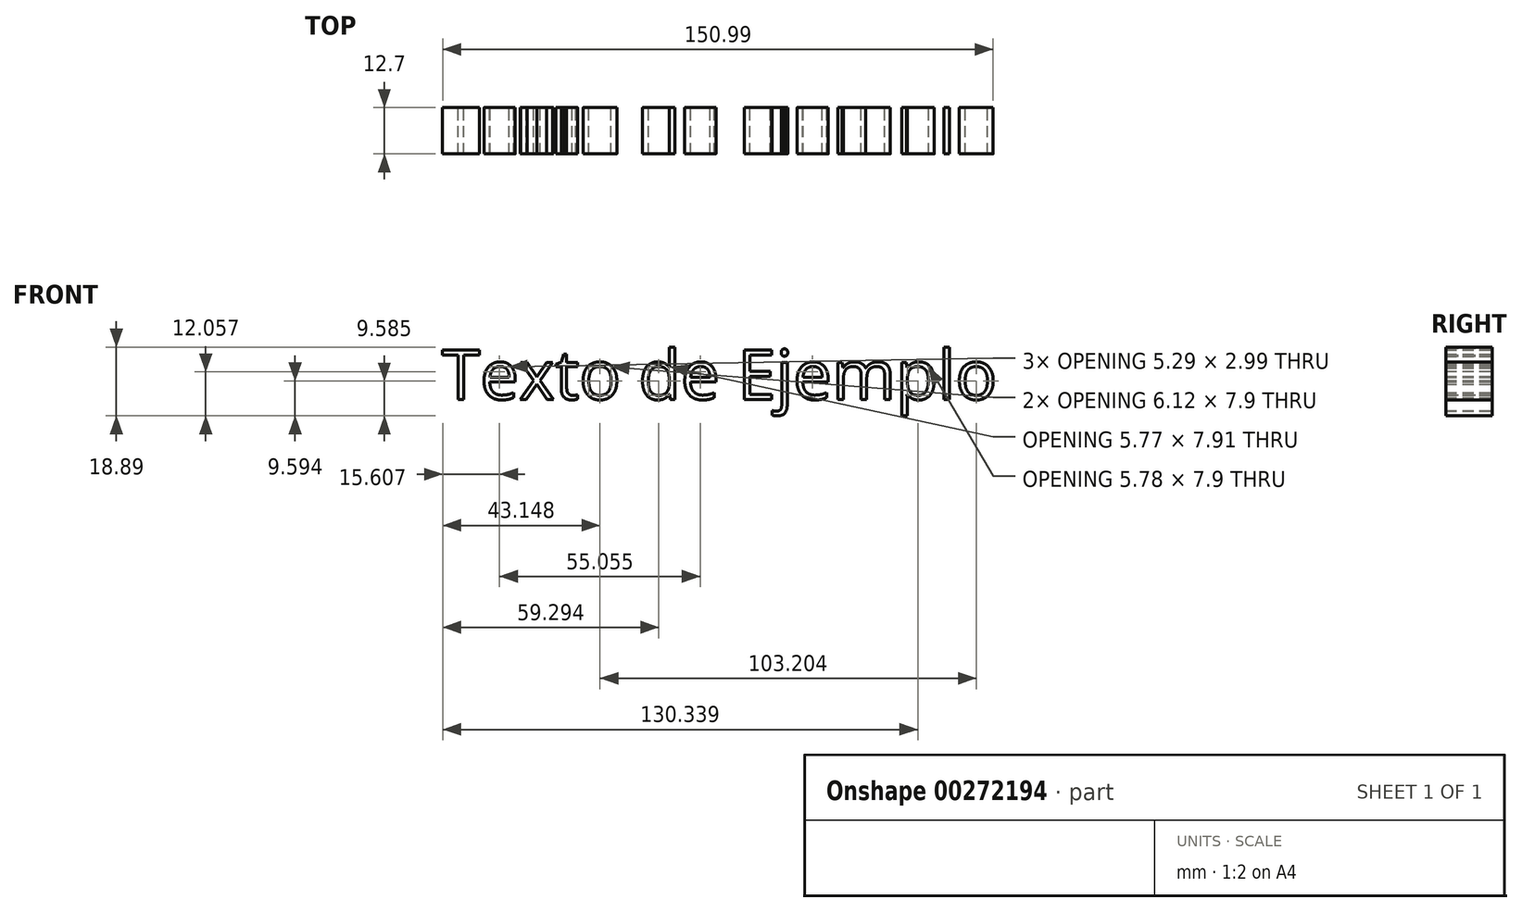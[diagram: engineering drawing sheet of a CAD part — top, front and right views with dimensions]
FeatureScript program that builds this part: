
annotation { "Feature Type Name" : "Feature", "Feature Type Description" : "" }
export const myFeature = defineFeature(function(context is Context, id is Id, definition is map)
    precondition{}
    {
        {
            var Q0;
            Q0=qCreatedBy(makeId("Front.planeOp"),FACE);
            var sketch = newSketch(context, id + "F0", { "sketchPlane" : qUnion([Q0])});
            skText(sketch, "E0", { "text": "Texto de Ejemplo", "fontName": "OpenSans-Regular.ttf"});
            const initialGuessF0  = {"E0": [-0.0762, -0.00436, 1, 0, 0.0136]};
            skSetInitialGuess(sketch, initialGuessF0);
            skSolve(sketch);
        }
        {
            var Q0;
            Q0 = qSketchRegion(id + "F0", true);
            extrude(context, id + "F1", {"entities" : qUnion([Q0]), "depth" : 12.7 * mm});
        }
    });
